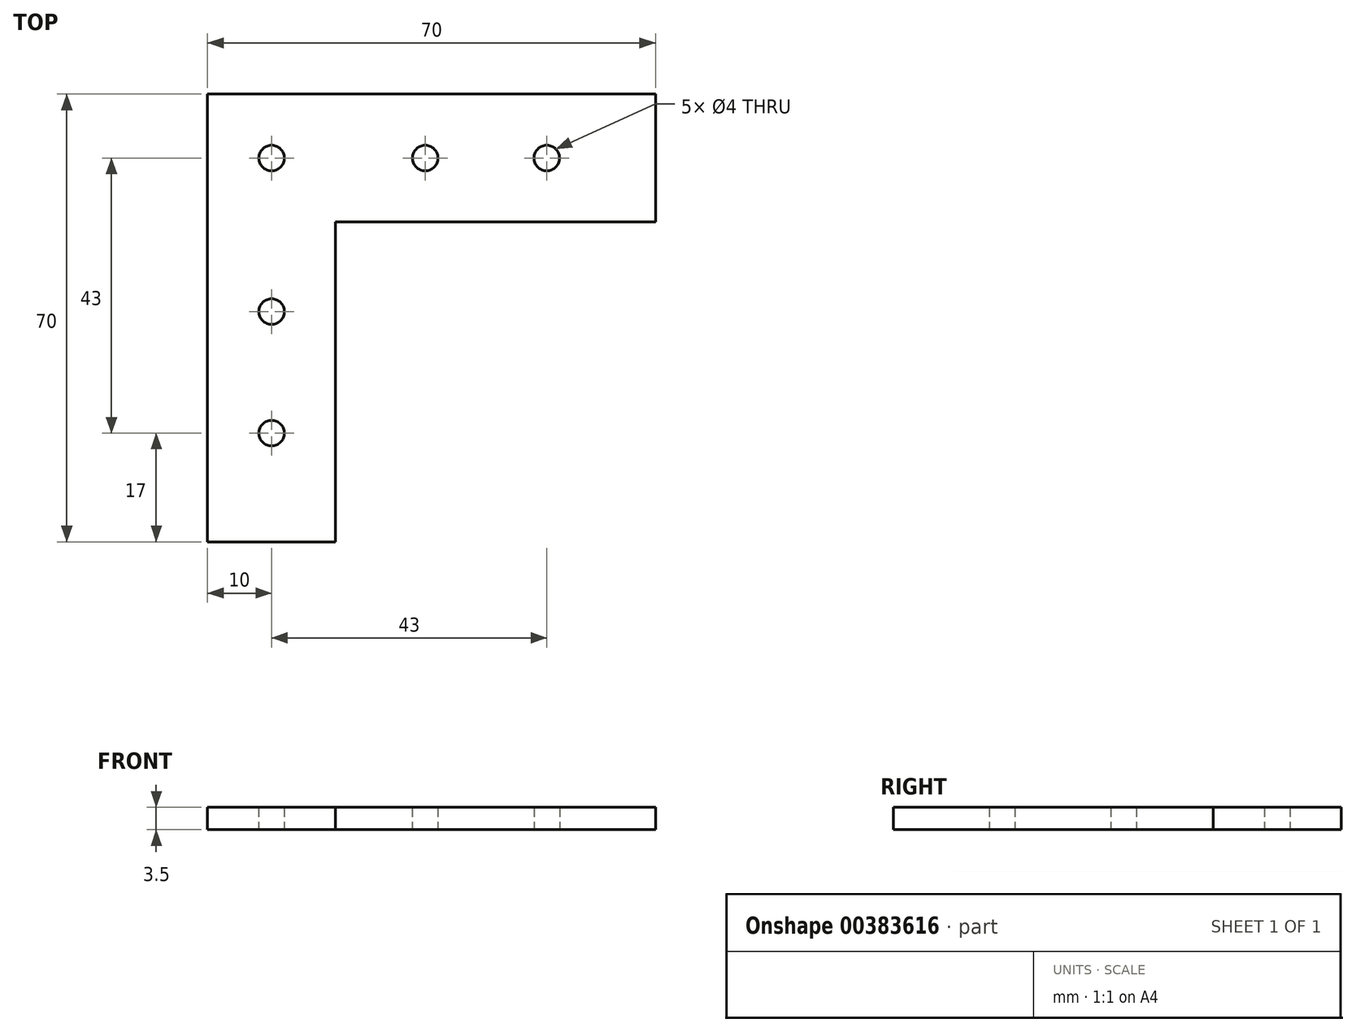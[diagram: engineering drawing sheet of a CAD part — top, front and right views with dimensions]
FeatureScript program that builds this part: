
annotation { "Feature Type Name" : "Feature", "Feature Type Description" : "" }
export const myFeature = defineFeature(function(context is Context, id is Id, definition is map)
    precondition{}
    {
        {
            var Q0;
            Q0=qCreatedBy(makeId("Top.planeOp"),FACE);
            var sketch = newSketch(context, id + "F0", { "sketchPlane" : qUnion([Q0])});
            skLineSegment(sketch, "E0.bottom", {"start": v(-10, -60) * mm, "end": v(10, -60) * mm});
            skLineSegment(sketch, "E0.top", {"start": v(-10, 10) * mm, "end": v(10, 10) * mm});
            skLineSegment(sketch, "E0.left", {"start": v(-10, -60) * mm, "end": v(-10, 10) * mm});
            skLineSegment(sketch, "E0.right", {"start": v(10, -60) * mm, "end": v(10, -10) * mm});
            skLineSegment(sketch, "E1.bottom", {"start": v(-10, 10) * mm, "end": v(60, 10) * mm});
            skLineSegment(sketch, "E1.top", {"start": v(10, -10) * mm, "end": v(60, -10) * mm});
            skLineSegment(sketch, "E1.left", {"start": v(-10, 10) * mm, "end": v(-10, -10) * mm});
            skLineSegment(sketch, "E1.right", {"start": v(60, 10) * mm, "end": v(60, -10) * mm});
            skLineSegment(sketch, "E2", {"start": v(60, 0) * mm, "end": v(-10, 0) * mm, "construction": true});
            skLineSegment(sketch, "E3", {"start": v(0, -60) * mm, "end": v(0, 10) * mm, "construction": true});
            skLineSegment(sketch, "E4", {"start": v(10, -10) * mm, "end": v(-10, -10) * mm, "construction": true});
            skLineSegment(sketch, "E5", {"start": v(10, 10) * mm, "end": v(10, -10) * mm, "construction": true});
            skPoint(sketch, "E6", {"position": v(0, 0) * mm});
            skPoint(sketch, "E7", {"position": v(0, -43) * mm});
            skPoint(sketch, "E8", {"position": v(0, -24) * mm});
            skPoint(sketch, "E9", {"position": v(43, 0) * mm});
            skCircle(sketch, "E10", {"center": v(43, 0) * mm, "radius": 2 * mm});
            skCircle(sketch, "E11", {"center": v(0, -24) * mm, "radius": 2 * mm});
            skCircle(sketch, "E12", {"center": v(0, -43) * mm, "radius": 2 * mm});
            skPoint(sketch, "E13", {"position": v(24, 0) * mm});
            skCircle(sketch, "E14", {"center": v(24, 0) * mm, "radius": 2 * mm});
            skCircle(sketch, "E15", {"center": v(0, 0) * mm, "radius": 2 * mm});
            skSolve(sketch);
        }
        {
            var Q0;
            Q0=makeQuery(id+"F0.imprint","IMPRINT",FACE,{"disambiguationData":[TD([[makeQuery(id+"F0.imprint","IMPRINT",EDGE,{"derivedFrom":sQuery(id+"F0.wireOp",EDGE,"E0.bottom")}),1.0]])]});
            extrude(context, id + "F1", {"entities" : qUnion([Q0]), "depth" : 3.5 * mm});
        }
    });
